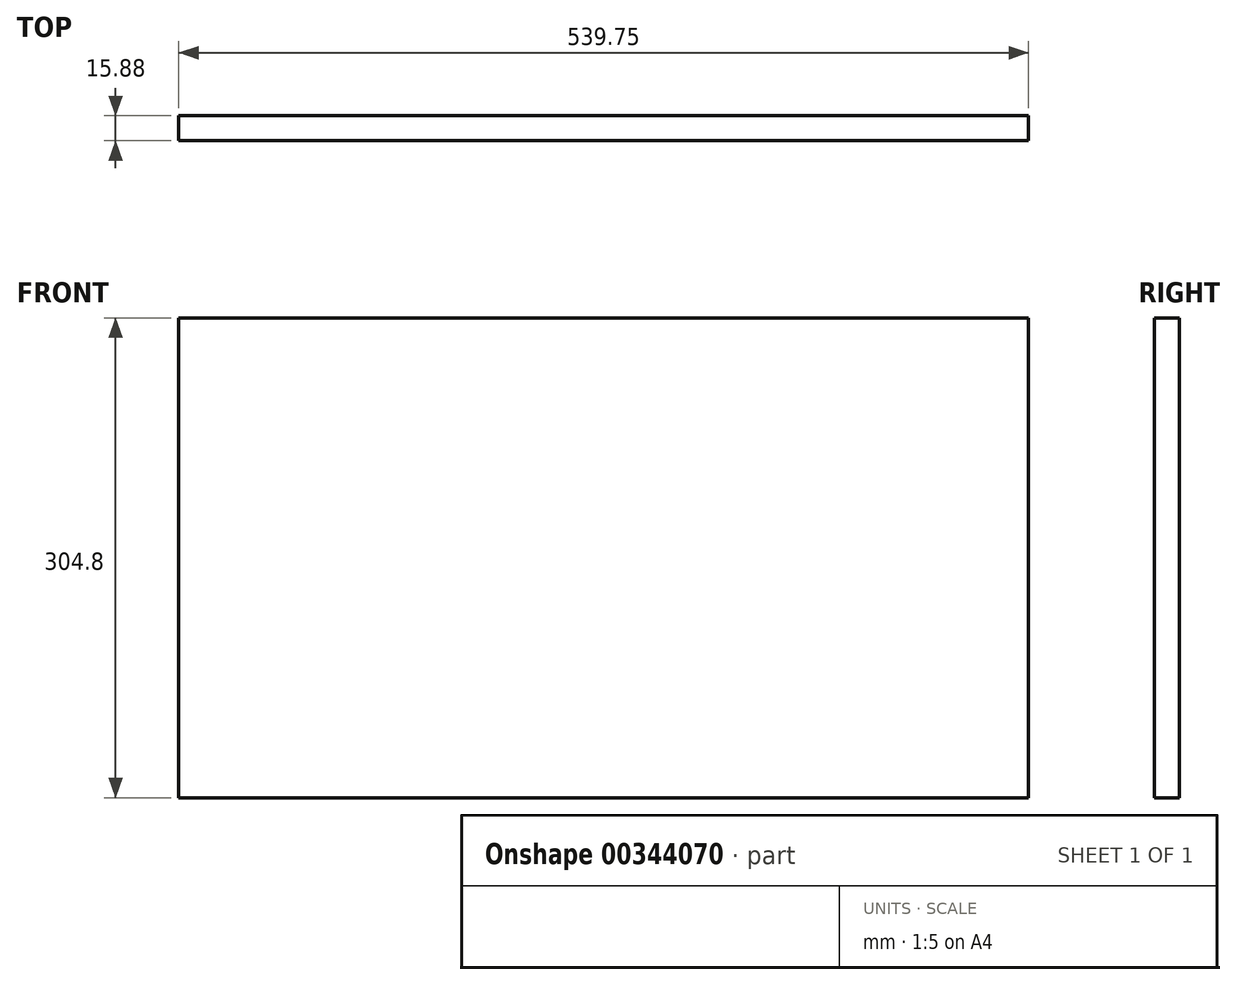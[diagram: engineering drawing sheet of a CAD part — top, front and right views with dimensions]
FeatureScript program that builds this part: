
annotation { "Feature Type Name" : "Feature", "Feature Type Description" : "" }
export const myFeature = defineFeature(function(context is Context, id is Id, definition is map)
    precondition{}
    {
        {
            var Q0;
            Q0=qCreatedBy(makeId("Front.planeOp"),FACE);
            var sketch = newSketch(context, id + "F0", { "sketchPlane" : qUnion([Q0])});
            skLineSegment(sketch, "E0.bottom", {"start": v(0, 0) * mm, "end": v(539.75, 0) * mm});
            skLineSegment(sketch, "E0.top", {"start": v(0, 304.8) * mm, "end": v(539.75, 304.8) * mm});
            skLineSegment(sketch, "E0.left", {"start": v(0, 0) * mm, "end": v(0, 304.8) * mm});
            skLineSegment(sketch, "E0.right", {"start": v(539.75, 0) * mm, "end": v(539.75, 304.8) * mm});
            skSolve(sketch);
        }
        {
            var Q0;
            Q0 = qSketchRegion(id + "F0", true);
            extrude(context, id + "F1", {"entities" : qUnion([Q0]), "depth" : 15.88 * mm});
        }
    });
